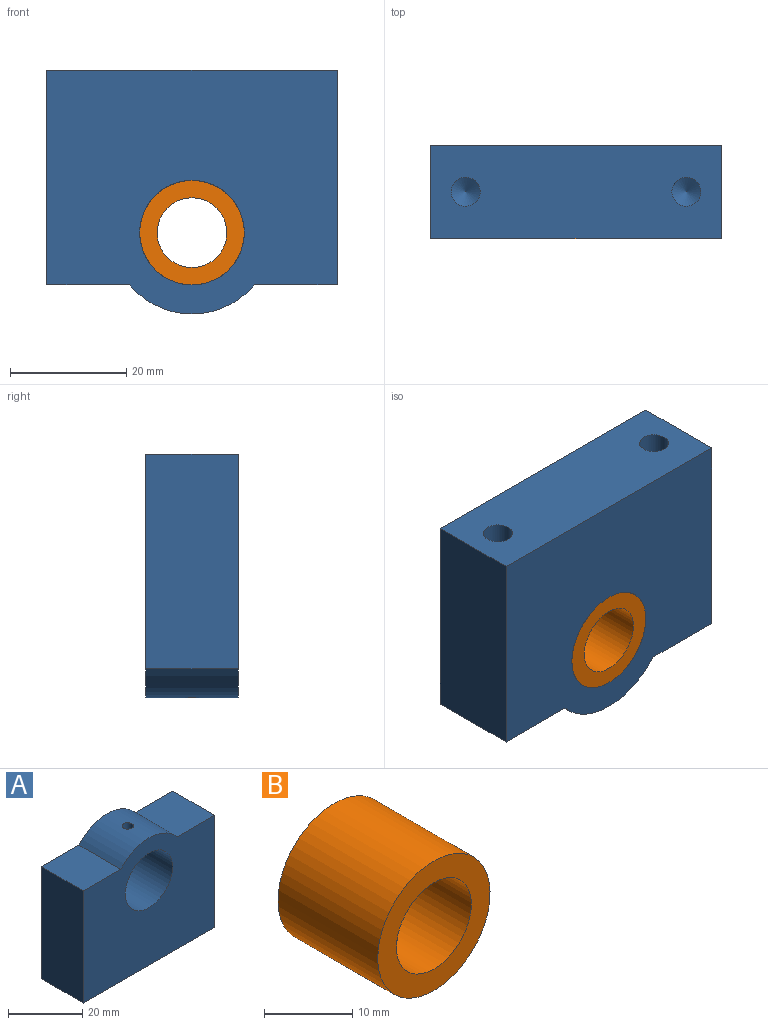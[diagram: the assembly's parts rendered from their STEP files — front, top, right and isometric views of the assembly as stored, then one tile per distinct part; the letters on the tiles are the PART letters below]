
ASSEMBLY  parts=2 mates=1
PART A: 14 faces, bbox 50x16x42 mm
  f0: plane 37x16mm, normal (-1,0,0), area 592mm2, adj f1,f5,f7,f8
  f1: plane 50x16mm, normal (0,0,-1), area 760.7mm2, adj f0,f2,f7,f8,f10,f12
  f2: plane 37x16mm, normal (1,0,0), area 592mm2, adj f1,f3,f7,f8
  f3: plane 16x14.28mm, normal (0,0,1), area 228.4mm2, adj f2,f4,f7,f8
  f4: cylinder r=14mm len=21.45mm, axis (0,1,0), area 383.8mm2, adj f3,f5,f7,f8,f13
  f5: plane 16x14.28mm, normal (0,0,1), area 228.4mm2, adj f0,f4,f7,f8
  f6: cylinder r=9mm len=18mm, axis (0,1,0), area 897.7mm2, adj f7,f8,f13
  f7: plane 50x42mm, normal (0,-1,0), area 1670mm2, adj f0,f1,f2,f3,f4,f5,f6
  f8: plane 50x42mm, normal (0,1,0), area 1670mm2, adj f0,f1,f2,f3,f4,f5,f6
  f9: cone r=0mm half-angle=59deg, axis (0,0,-1), area 22.9mm2, adj f10
  f10: cylinder r=2.5mm len=10mm, axis (0,0,-1), area 157.1mm2, adj f1,f9
  f11: cone r=0mm half-angle=59deg, axis (0,0,-1), area 22.9mm2, adj f12
  f12: cylinder r=2.5mm len=10mm, axis (0,0,-1), area 157.1mm2, adj f1,f11
  f13: cylinder r=1.5mm len=5.13mm, axis (0,0,1), area 47.3mm2, adj f4,f6
PART B: 5 faces, bbox 18x16x18 mm
  f0: cylinder r=6mm len=16mm, axis (0,1,0), area 596.1mm2, adj f2,f3,f4
  f1: cylinder r=9mm len=18mm, axis (0,1,0), area 897.7mm2, adj f2,f3,f4
  f2: plane 18x18mm, normal (0,-1,0), area 141.4mm2, adj f0,f1
  f3: plane 18x18mm, normal (0,1,0), area 141.4mm2, adj f0,f1
  f4: cylinder r=1.5mm len=3.19mm, axis (0,0,1), area 28.6mm2, adj f0,f1
PLACE A rot(axis=(0,1,0),180deg) t=(74.07,33.68,-6.98)mm
PLACE B t=(109.26,33.68,-86.97)mm
MATE revolute A.f4 <-> B.f0  axis (0,1,0) through (49.07,33.68,-34.98)mm
